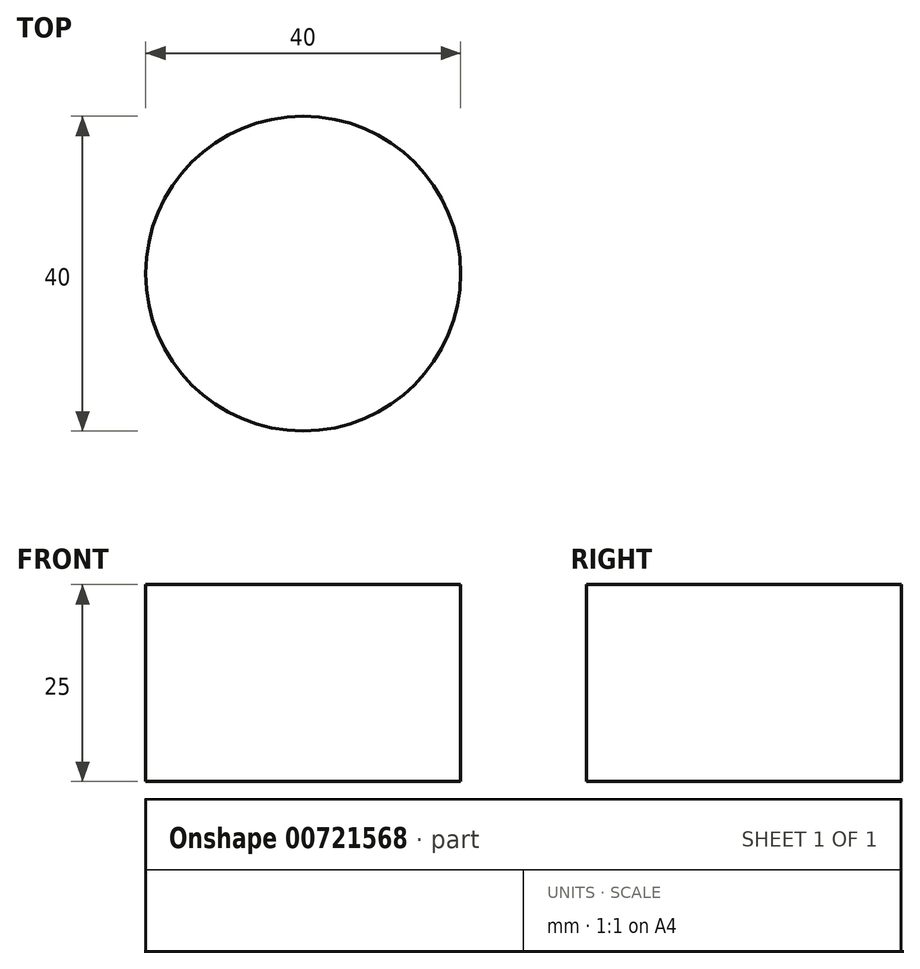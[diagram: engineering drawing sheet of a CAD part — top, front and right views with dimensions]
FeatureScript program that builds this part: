
annotation { "Feature Type Name" : "Feature", "Feature Type Description" : "" }
export const myFeature = defineFeature(function(context is Context, id is Id, definition is map)
    precondition{}
    {
        {
            var Q0;
            Q0=qCreatedBy(makeId("Top.planeOp"),FACE);
            var sketch = newSketch(context, id + "F0", { "sketchPlane" : qUnion([Q0])});
            skCircle(sketch, "E0", {"center": v(0, 0) * mm, "radius": 20 * mm});
            skSolve(sketch);
        }
        {
            var Q0;
            Q0 = qSketchRegion(id + "F0", true);
            extrude(context, id + "F1", {"entities" : qUnion([Q0]), "depth" : 25 * mm, "offsetDistance" : 25 * mm});
        }
    });
